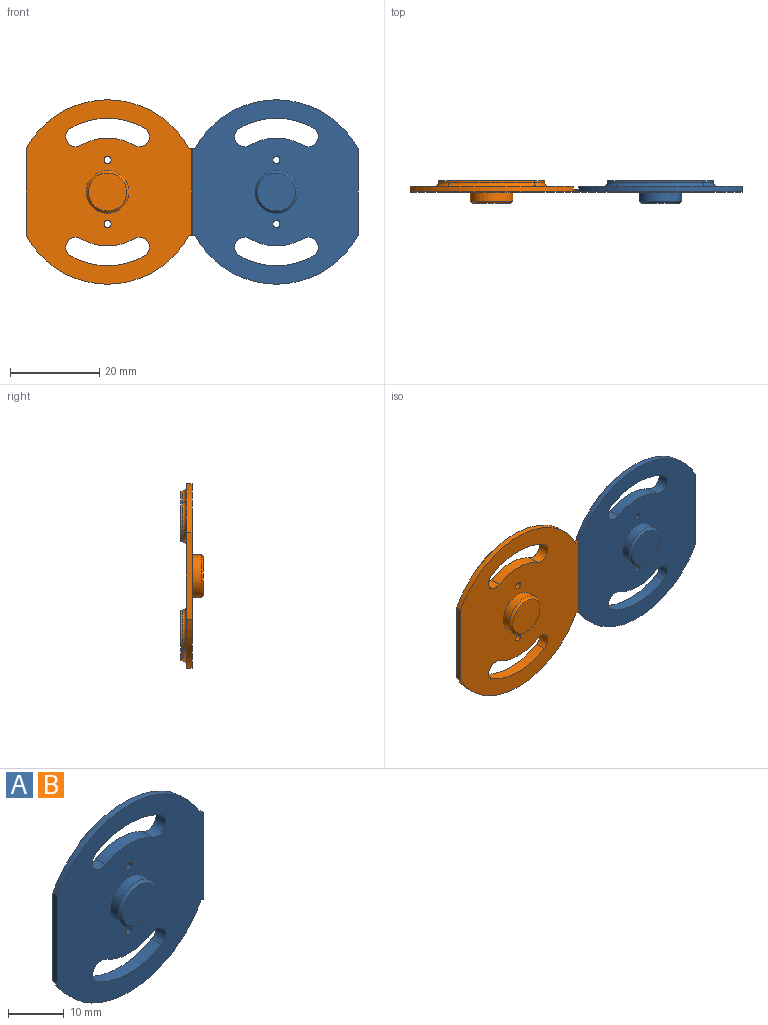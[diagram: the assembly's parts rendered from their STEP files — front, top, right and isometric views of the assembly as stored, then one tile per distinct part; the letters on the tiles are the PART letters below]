
ASSEMBLY  parts=2 mates=1
PART A: 41 faces, bbox 37.1x5.2x44.2 mm
  f0: plane 19.25x0.64mm, normal (1,0,0), area 12.2mm2, adj f1,f3,f4,f37
  f1: cylinder r=20.64mm len=36.51mm, axis (0,1,0), area 56.9mm2, adj f0,f2,f3,f35,f39
  f2: plane 41.28x37.15mm, normal (0,-1,0), area 1049.1mm2, adj f1,f4,f5,f7,f14,f15,f16,f17
  f3: plane 41.28x36.51mm, normal (0,1,0), area 745.7mm2, adj f0,f1,f4,f5,f18,f19,f20,f21
  f4: cylinder r=20.64mm len=36.51mm, axis (0,1,0), area 56.9mm2, adj f0,f2,f3,f35,f38
  f5: cylinder r=0.79mm len=1.59mm, axis (0,1,0), area 6.3mm2, adj f2,f3
  f6: plane 23.81x11.44mm, normal (0,1,0), area 131.7mm2, adj f22,f23,f24,f25,f26,f27,f28,f29
  f7: cylinder r=4.76mm len=9.53mm, axis (0,1,0), area 60.8mm2, adj f2,f36
  f8: plane 8.51x8.51mm, normal (0,-1,0), area 56.9mm2, adj f36
  f9: cylinder r=19.05mm len=19.05mm, axis (0,-1,0), area 9.5mm2, adj f10,f12,f13,f21
  f10: cylinder r=4.76mm len=8.89mm, axis (0,-1,0), area 7.1mm2, adj f9,f11,f13,f19
  f11: cylinder r=9.53mm len=9.53mm, axis (0,-1,0), area 4.8mm2, adj f10,f12,f13,f18
  f12: cylinder r=4.76mm len=8.89mm, axis (0,-1,0), area 7.1mm2, adj f9,f11,f13,f20
  f13: plane 23.81x11.44mm, normal (0,1,0), area 131.7mm2, adj f9,f10,f11,f12,f14,f15,f16,f17
  f14: cylinder r=2.22mm len=4.15mm, axis (0,1,0), area 17.7mm2, adj f2,f13,f15,f16
  f15: cylinder r=16.51mm len=16.51mm, axis (0,1,0), area 43.9mm2, adj f2,f13,f14,f17
  f16: cylinder r=12.06mm len=12.07mm, axis (0,1,0), area 32.1mm2, adj f2,f13,f14,f17
  f17: cylinder r=2.22mm len=4.15mm, axis (0,1,0), area 17.7mm2, adj f2,f13,f15,f16
  f18: torus R=8.73mm, axis (0,-1,0), area 12.1mm2, adj f3,f11,f19,f20
  f19: torus R=5.56mm, axis (0,-1,0), area 19.8mm2, adj f3,f10,f18,f21
  f20: torus R=5.56mm, axis (0,-1,0), area 19.8mm2, adj f3,f12,f18,f21
  f21: torus R=19.84mm, axis (0,-1,0), area 25.2mm2, adj f3,f9,f19,f20
  f22: cylinder r=19.05mm len=19.05mm, axis (0,-1,0), area 9.5mm2, adj f6,f23,f25,f33
  f23: cylinder r=4.76mm len=8.89mm, axis (0,-1,0), area 7.1mm2, adj f6,f22,f24,f32
  f24: cylinder r=9.53mm len=9.53mm, axis (0,-1,0), area 4.8mm2, adj f6,f23,f25,f30
  f25: cylinder r=4.76mm len=8.89mm, axis (0,-1,0), area 7.1mm2, adj f6,f22,f24,f31
  f26: cylinder r=16.51mm len=16.51mm, axis (0,1,0), area 43.9mm2, adj f2,f6,f27,f29
  f27: cylinder r=2.22mm len=4.15mm, axis (0,1,0), area 17.7mm2, adj f2,f6,f26,f28
  f28: cylinder r=12.06mm len=12.07mm, axis (0,1,0), area 32.1mm2, adj f2,f6,f27,f29
  f29: cylinder r=2.22mm len=4.15mm, axis (0,1,0), area 17.7mm2, adj f2,f6,f26,f28
  f30: torus R=8.73mm, axis (0,-1,0), area 12.1mm2, adj f3,f24,f31,f32
  f31: torus R=5.56mm, axis (0,-1,0), area 19.8mm2, adj f3,f25,f30,f33
  f32: torus R=5.56mm, axis (0,-1,0), area 19.8mm2, adj f3,f23,f30,f33
  f33: torus R=19.84mm, axis (0,-1,0), area 25.2mm2, adj f3,f22,f31,f32
  f34: cylinder r=0.79mm len=1.59mm, axis (0,1,0), area 6.3mm2, adj f2,f3
  f35: plane 19.25x1.27mm, normal (-1,0,0), area 24.4mm2, adj f1,f2,f3,f4
  f36: cone r=4.25mm half-angle=45deg, axis (0,1,0), area 20.4mm2, adj f7,f8
  f37: plane 19.25x0.64mm, normal (0,1,0), area 12.2mm2, adj f0,f38,f39,f40
  f38: plane 0.64x0.64mm, normal (0,0,1), area 0.4mm2, adj f2,f4,f37,f40
  f39: plane 0.64x0.64mm, normal (0,0,-1), area 0.4mm2, adj f1,f2,f37,f40
  f40: plane 19.25x0.64mm, normal (1,0,0), area 12.2mm2, adj f2,f37,f38,f39
PART B: same geometry as A
PLACE A rot(axis=(0,1,0),180deg) t=(37.78,0,0)mm
PLACE B at identity fixed
MATE fastened B.f40 <-> A.f40  axis (1,0,0) through (18.89,-0.95,0)mm
